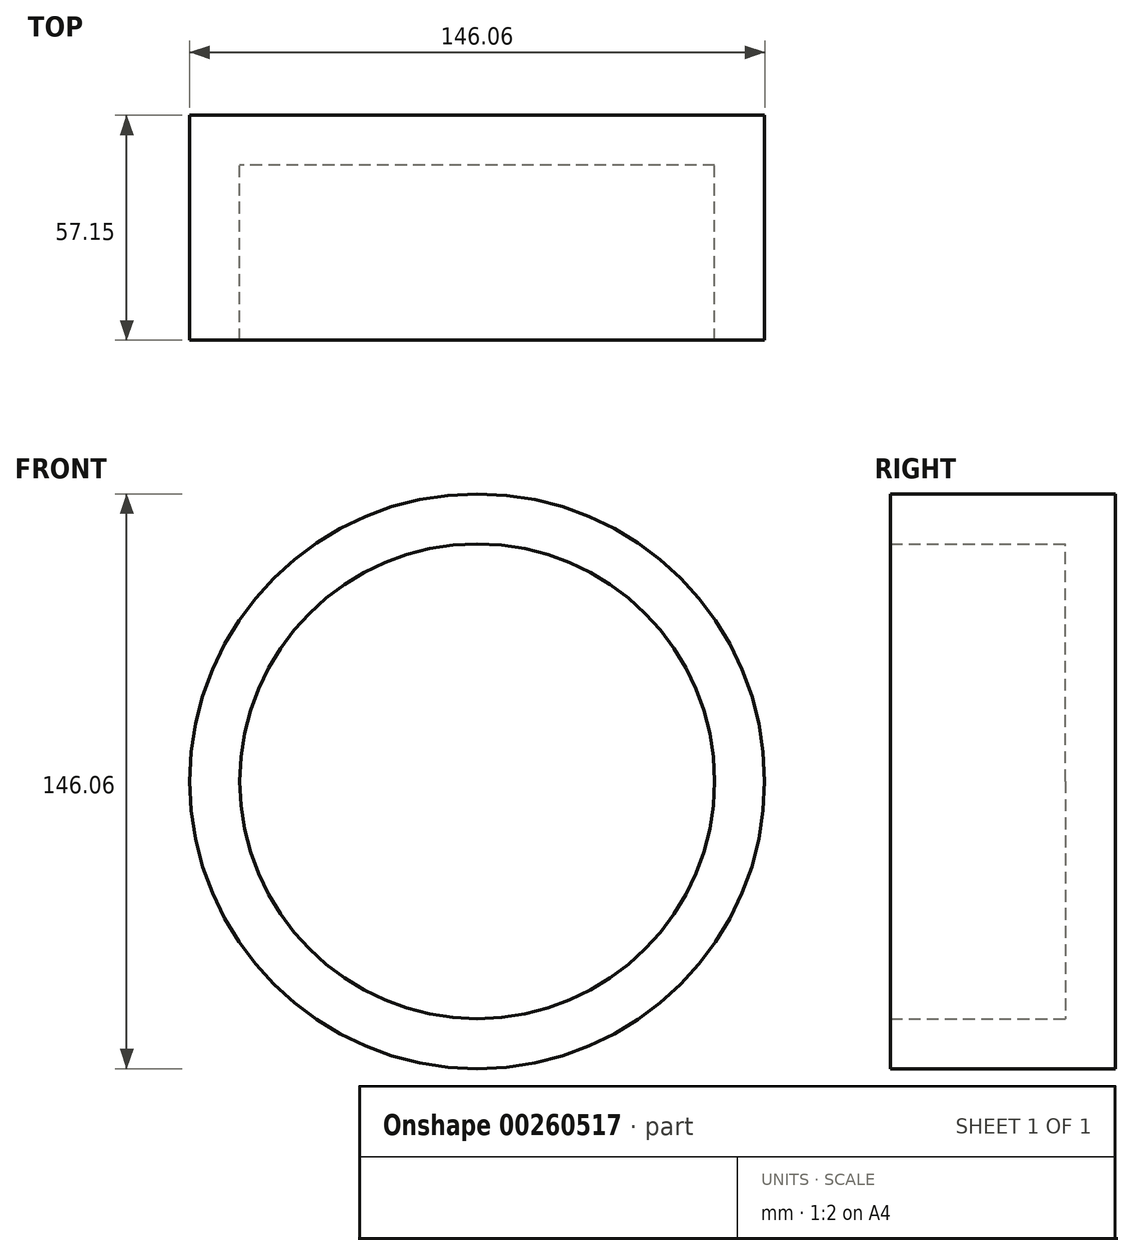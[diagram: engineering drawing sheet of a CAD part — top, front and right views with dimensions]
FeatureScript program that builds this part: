
annotation { "Feature Type Name" : "Feature", "Feature Type Description" : "" }
export const myFeature = defineFeature(function(context is Context, id is Id, definition is map)
    precondition{}
    {
        {
            var Q0;
            Q0=qCreatedBy(makeId("Front.planeOp"),FACE);
            var sketch = newSketch(context, id + "F0", { "sketchPlane" : qUnion([Q0])});
            skCircle(sketch, "E0", {"center": v(0, 0) * mm, "radius": 73.03 * mm});
            skLineSegment(sketch, "E1", {"start": v(73.03, 0) * mm, "end": v(60.33, 0) * mm});
            skCircle(sketch, "E2", {"center": v(0, 0) * mm, "radius": 60.33 * mm});
            skLineSegment(sketch, "E3.left", {"start": v(-60.33, 0) * mm, "end": v(-60.33, 0) * mm});
            skLineSegment(sketch, "E3.right", {"start": v(60.33, 0) * mm, "end": v(60.33, 0) * mm});
            skLineSegment(sketch, "E4.bottom", {"start": v(60.33, 0) * mm, "end": v(-60.32, 0) * mm});
            skLineSegment(sketch, "E4.top", {"start": v(60.32, 0) * mm, "end": v(-60.33, 0) * mm});
            skSolve(sketch);
        }
        {
            var Q0;
            Q0=makeQuery(id+"F0.imprint","IMPRINT",FACE,{"disambiguationData":[TD([[makeQuery(id+"F0.imprint","IMPRINT",EDGE,{"derivedFrom":sQuery(id+"F0.wireOp",EDGE,"E0")}),1.0]])]});
            extrude(context, id + "F1", {"entities" : qUnion([Q0]), "depth" : 57.15 * mm});
        }
        {
            var Q0;
            Q0=makeQuery(id+"F0.imprint","IMPRINT",FACE,{"disambiguationData":[TD([[makeQuery(id+"F0.imprint","IMPRINT",EDGE,{"derivedFrom":sQuery(id+"F0.wireOp",EDGE,"E2")}),1.0]])]});
            extrude(context, id + "F2", {"entities" : qUnion([Q0]), "operationType" : NewBodyOperationType.ADD, "depth" : 12.7 * mm});
        }
        {
            var Q0;
            Q0=sQuery(id+"F0.wireOp",EDGE,"E4.top");
            extrude(context, id + "F3", {"bodyType" : ToolBodyType.SURFACE, "surfaceEntities" : qUnion([Q0]), "depth" : 57.15 * mm});
        }
    });
